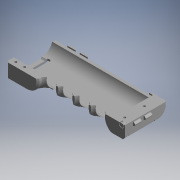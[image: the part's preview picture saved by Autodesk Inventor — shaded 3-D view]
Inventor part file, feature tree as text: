
AUTODESK INVENTOR PART (.ipt)
format: ipt  version: 2018 (Build 220112000, 112)  size: 1,735,168 bytes
history: native  units: mm
features: other x2, projected_geometry x2, extrude x1, sketch x1
ambient origin geometry x8: Origin, YZ Plane, XZ Plane, XY Plane, X Axis, Y Axis, Z Axis, Center Point
bodies: Body1 (feature_tree), Body2 (feature_tree)
feature tree (6):
  other  "ソリッド2"
  extrude  "押し出し1"  Depth=10.0mm TaperAngle=0.0deg
  sketch  "スケッチ1"
  projected_geometry  "投影ループ1"
  projected_geometry  "投影ループ2"
  other  "ソリッド1"
